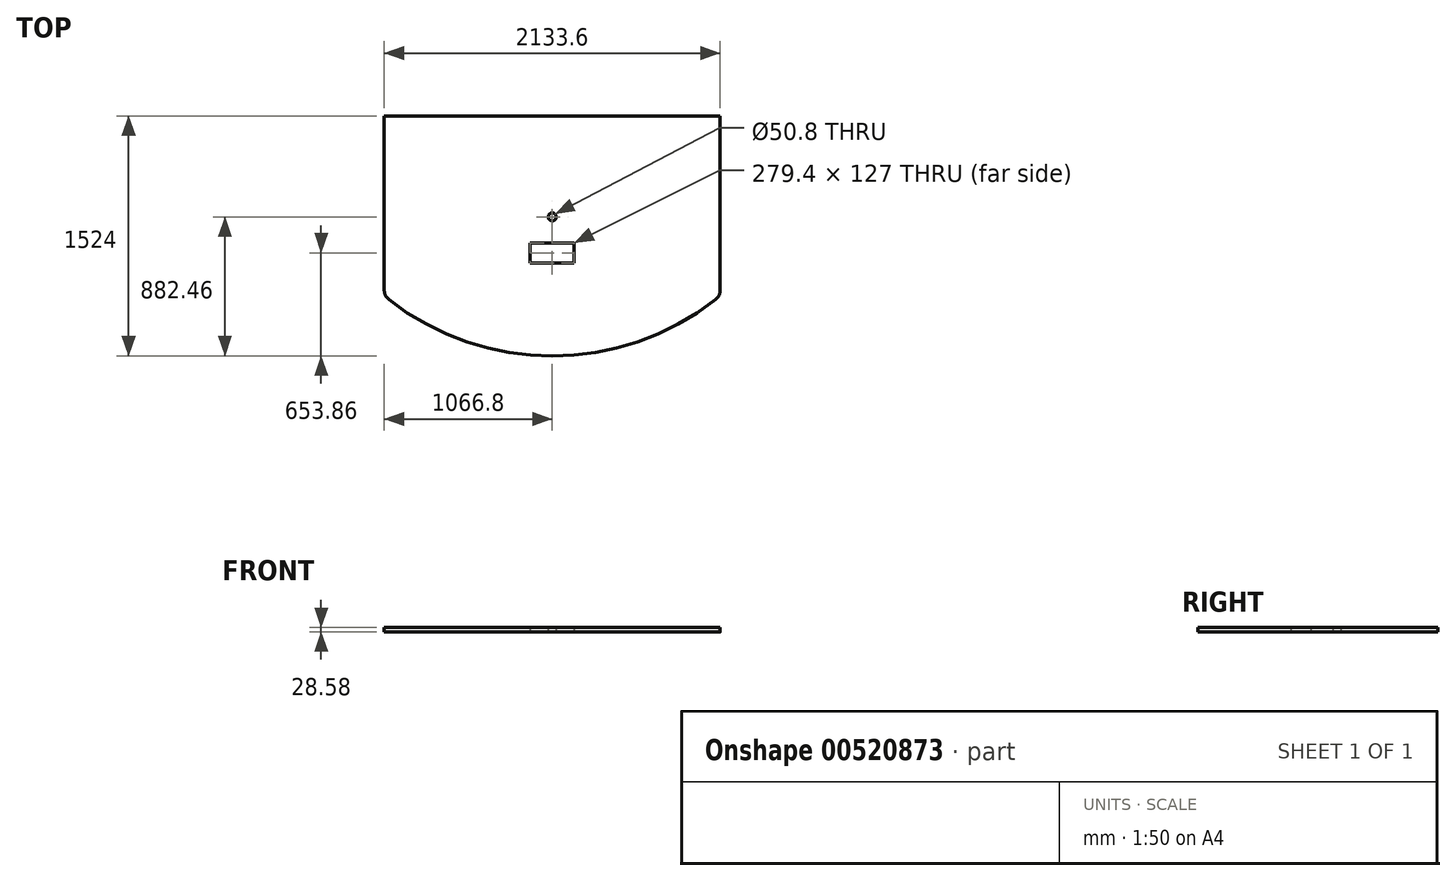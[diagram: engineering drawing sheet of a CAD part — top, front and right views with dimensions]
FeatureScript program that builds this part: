
annotation { "Feature Type Name" : "Feature", "Feature Type Description" : "" }
export const myFeature = defineFeature(function(context is Context, id is Id, definition is map)
    precondition{}
    {
        {
            var Q0;
            Q0=qCreatedBy(makeId("Top.planeOp"),FACE);
            var sketch = newSketch(context, id + "F0", { "sketchPlane" : qUnion([Q0])});
            skPoint(sketch, "E0.middle", {"position": v(0, 0) * mm});
            skLineSegment(sketch, "E1", {"start": v(0, 0) * mm, "end": v(0, 0) * mm});
            skPoint(sketch, "E1.endSnap0", {"position": v(0, 63.5) * mm});
            skCircle(sketch, "E2", {"center": v(0, 0) * mm, "radius": 25.4 * mm});
            skLineSegment(sketch, "E3.top", {"start": v(-1066.8, -882.46) * mm, "end": v(1066.8, -882.46) * mm});
            skLineSegment(sketch, "E4", {"start": v(-1066.8, -44.26) * mm, "end": v(-1066.8, -464.85) * mm});
            skLineSegment(sketch, "E5", {"start": v(1066.8, -44.26) * mm, "end": v(1066.8, -464.85) * mm});
            skLineSegment(sketch, "E6", {"start": v(0, -882.46) * mm, "end": v(0, -12.7) * mm});
            skArc(sketch, "E7", {"start": v(-1037.55, -524.87) * mm, "mid": v(0, -882.46) * mm, "end": v(1037.55, -524.87) * mm});
            skPoint(sketch, "E8.visualSharp", {"position": v(-1066.8, -501.46) * mm});
            skArc(sketch, "E8.filletArc", {"start": v(-1066.8, -464.85) * mm, "mid": v(-1059.1, -498.23) * mm, "end": v(-1037.55, -524.87) * mm});
            skPoint(sketch, "E9.visualSharp", {"position": v(1066.8, -501.46) * mm});
            skArc(sketch, "E9.filletArc", {"start": v(1037.55, -524.87) * mm, "mid": v(1059.1, -498.23) * mm, "end": v(1066.8, -464.85) * mm});
            skLineSegment(sketch, "E10.top", {"start": v(-1066.8, 641.54) * mm, "end": v(1066.8, 641.54) * mm});
            skLineSegment(sketch, "E11", {"start": v(-1066.8, -44.26) * mm, "end": v(-1066.8, 641.54) * mm});
            skLineSegment(sketch, "E12", {"start": v(1066.8, -44.26) * mm, "end": v(1066.8, 641.54) * mm});
            skLineSegment(sketch, "E13", {"start": v(0, 0) * mm, "end": v(0, -228.6) * mm});
            skLineSegment(sketch, "E14.bottom", {"start": v(-139.7, -165.1) * mm, "end": v(139.7, -165.1) * mm});
            skLineSegment(sketch, "E14.top", {"start": v(-139.7, -292.1) * mm, "end": v(139.7, -292.1) * mm});
            skLineSegment(sketch, "E14.left", {"start": v(-139.7, -165.1) * mm, "end": v(-139.7, -292.1) * mm});
            skLineSegment(sketch, "E14.right", {"start": v(139.7, -165.1) * mm, "end": v(139.7, -292.1) * mm});
            skPoint(sketch, "E14.middle", {"position": v(0, -228.6) * mm});
            skSolve(sketch);
        }
        {
            var Q0;
            {var subQ4=sQuery(id+"F0.wireOp",EDGE,"9nkhfROt-6ckf-Ddc5-qOw8-ZPpShEiKBqfZ.left");Q0=makeQuery(id+"F0.imprint","IMPRINT",FACE,{"disambiguationData":[TD([[makeQuery(id+"F0.imprint","IMPRINT",EDGE,{"derivedFrom":subQ4}),1.0]])]});}
            var Q1;
            Q1=makeQuery(id+"F0.imprint","IMPRINT",FACE,{"disambiguationData":[TD([[makeQuery(id+"F0.imprint","IMPRINT",EDGE,{"derivedFrom":sQuery(id+"F0.wireOp",EDGE,"E2")}),-1.0]])]});
            extrude(context, id + "F1", {"entities" : qUnion([Q0, Q1]), "depth" : 28.57 * mm, "offsetDistance" : 25.4 * mm});
        }
    });
